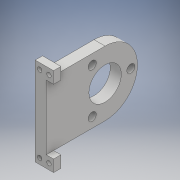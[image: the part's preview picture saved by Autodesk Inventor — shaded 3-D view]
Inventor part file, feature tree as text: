
AUTODESK INVENTOR PART (.ipt)
format: ipt  version: 2017 (Build 210142000, 142)  size: 178,176 bytes
history: native  units: mm
features: extrude x5, sketch x5
ambient origin geometry x8: Origin, YZ Plane, XZ Plane, XY Plane, X Axis, Y Axis, Z Axis, Center Point
bodies: Solid1 (feature_tree)
feature tree (10):
  extrude  "Extrusion1"  Depth=44.0mm
  extrude  "Extrusion2"  Depth=5.5mm
  extrude  "Extrusion3"  Depth=7.5mm TaperAngle=0.0deg
  extrude  "Extrusion5"  Depth=5.5mm
  extrude  "Extrusion7"  Depth=10.0mm TaperAngle=0.0deg
  sketch  "Sketch1"  dims[d0=22.0mm d1=44.0mm]
  sketch  "Sketch2"  dims[d2=35.0mm d3=5.5mm]
  sketch  "Sketch3"  dims[d4=30.0mm d6=360.0deg d8=7.5mm d9=0.0mm]
  sketch  "Sketch5"  dims[d10=35.0mm d11=5.5mm]
  sketch  "Sketch8"  dims[d12=30.0mm d14=360.0deg d16=10.0mm d17=0.0mm d18=40.0mm d19=90.0deg d20=50.0mm d21=25.0mm d22=5.0mm d23=30.0mm d24=5.0mm d25=60.0mm d26=5.0mm d27=7.5mm d28=0.0mm d41=5.0mm d42=12.5mm d43=0.0mm d44=0.0mm d55=5.0mm d56=0.0mm]
